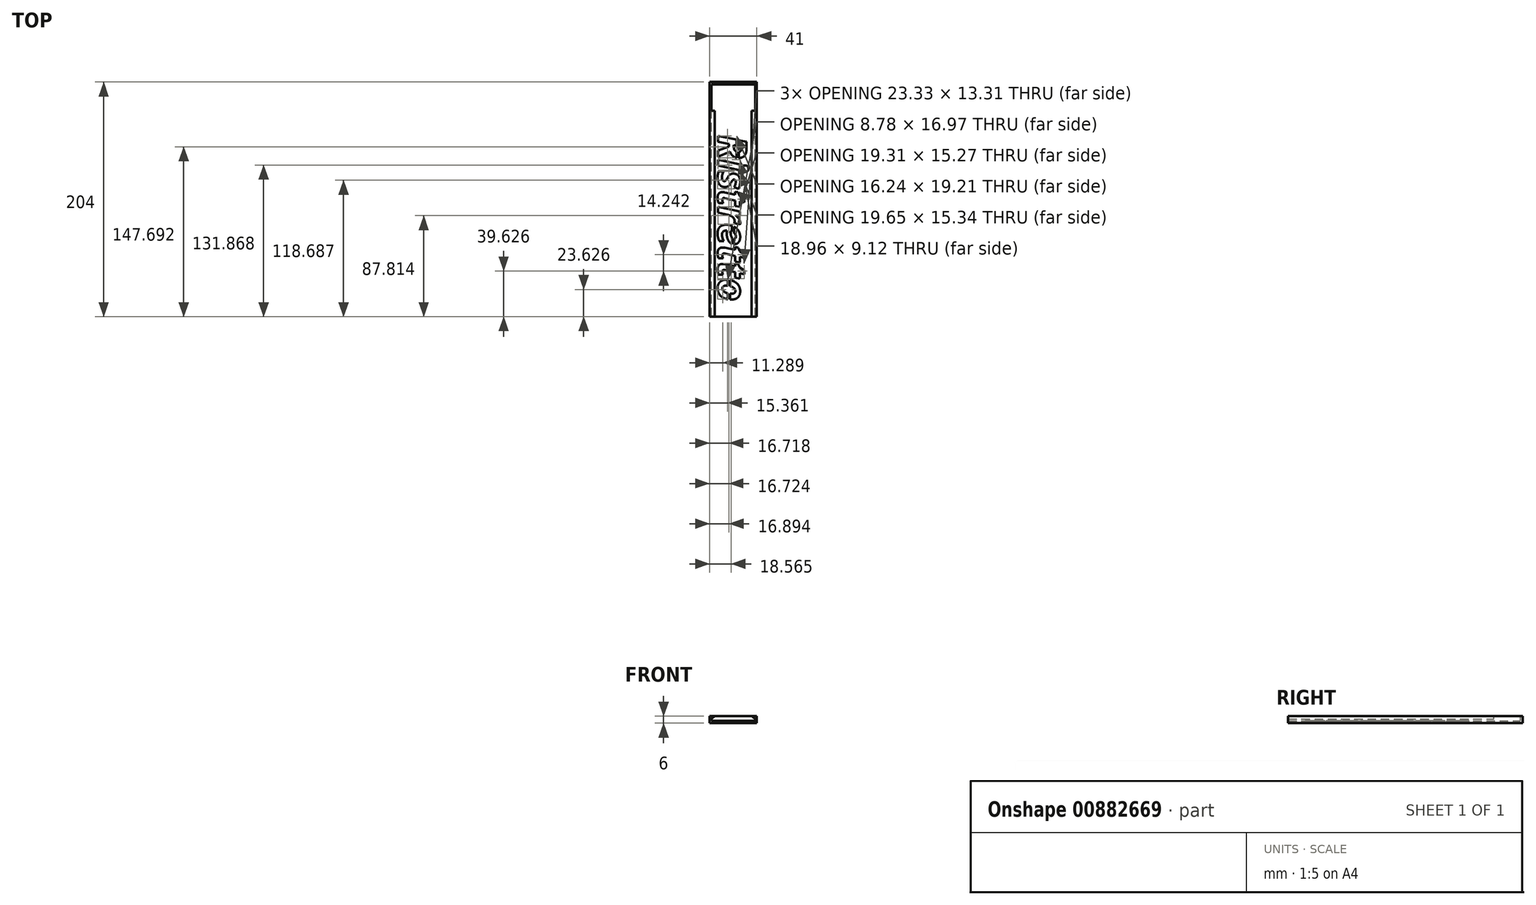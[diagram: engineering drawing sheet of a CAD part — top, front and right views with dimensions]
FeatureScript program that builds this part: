
annotation { "Feature Type Name" : "Feature", "Feature Type Description" : "" }
export const myFeature = defineFeature(function(context is Context, id is Id, definition is map)
    precondition{}
    {
        {
            var Q0;
            Q0=qCreatedBy(makeId("Front.planeOp"),FACE);
            var sketch = newSketch(context, id + "F0", { "sketchPlane" : qUnion([Q0])});
            skLineSegment(sketch, "E0", {"start": v(-20.5, 0) * mm, "end": v(20.5, 0) * mm});
            skLineSegment(sketch, "E1", {"start": v(20.5, 0) * mm, "end": v(20.5, 6) * mm});
            skLineSegment(sketch, "E2", {"start": v(20.5, 6) * mm, "end": v(16, 6) * mm});
            skLineSegment(sketch, "E3", {"start": v(19, 2) * mm, "end": v(-19, 2) * mm});
            skLineSegment(sketch, "E4", {"start": v(-16, 6) * mm, "end": v(-20.5, 6) * mm});
            skLineSegment(sketch, "E5", {"start": v(-20.5, 6) * mm, "end": v(-20.5, 0) * mm});
            skLineSegment(sketch, "E6", {"start": v(-16, 6) * mm, "end": v(16, 6) * mm});
            skLineSegment(sketch, "E7", {"start": v(16, 6) * mm, "end": v(19, 3.6) * mm});
            skLineSegment(sketch, "E8", {"start": v(19, 3.6) * mm, "end": v(19, 2) * mm});
            skLineSegment(sketch, "E9", {"start": v(-16, 6) * mm, "end": v(-19, 3.6) * mm});
            skLineSegment(sketch, "E10", {"start": v(-19, 3.6) * mm, "end": v(-19, 2) * mm});
            skSolve(sketch);
        }
        {
            var Q0;
            Q0=makeQuery(id+"F0.imprint","IMPRINT",FACE,{"disambiguationData":[TD([[makeQuery(id+"F0.imprint","IMPRINT",EDGE,{"derivedFrom":sQuery(id+"F0.wireOp",EDGE,"E0")}),1.0]])]});
            extrude(context, id + "F1", {"entities" : qUnion([Q0]), "depth" : 202 * mm, "offsetDistance" : 25 * mm});
        }
        {
            var Q0;
            Q0=qCreatedBy(makeId("Front.planeOp"),FACE);
            var sketch = newSketch(context, id + "F2", { "sketchPlane" : qUnion([Q0])});
            skLineSegment(sketch, "E11.bottom", {"start": v(20.5, 6) * mm, "end": v(-20.5, 6) * mm});
            skLineSegment(sketch, "E11.top", {"start": v(20.5, 0) * mm, "end": v(-20.5, 0) * mm});
            skLineSegment(sketch, "E11.left", {"start": v(20.5, 6) * mm, "end": v(20.5, 0) * mm});
            skLineSegment(sketch, "E11.right", {"start": v(-20.5, 6) * mm, "end": v(-20.5, 0) * mm});
            skSolve(sketch);
        }
        {
            var Q0;
            Q0=makeQuery(id+"F2.imprint","IMPRINT",FACE,{"disambiguationData":[TD([[makeQuery(id+"F2.imprint","IMPRINT",EDGE,{"derivedFrom":sQuery(id+"F2.wireOp",EDGE,"E11.bottom")}),1.0]])]});
            extrude(context, id + "F3", {"entities" : qUnion([Q0]), "operationType" : NewBodyOperationType.ADD, "oppositeDirection" : true, "depth" : 2 * mm, "offsetDistance" : 25 * mm});
        }
        {
            var Q0;
            Q0=makeQuery(id+"F3.boolean.opBoolean","MERGE",FACE,{"derivedFrom":[makeQuery(id+"F1.opExtrude","SWEPT_FACE",FACE,{"disambiguationData":[OSD([sQuery(id+"F0.wireOp",EDGE,"E2")])]}),makeQuery(id+"F1.opExtrude","SWEPT_FACE",FACE,{"disambiguationData":[OSD([sQuery(id+"F0.wireOp",EDGE,"E4")])]}),makeQuery(id+"F3.opExtrude","SWEPT_FACE",FACE,{"disambiguationData":[OSD([sQuery(id+"F2.wireOp",EDGE,"E11.bottom")])]})]});
            cPlane(context, id + "F4", {"entities" : qUnion([Q0]), "cplaneType" : CPlaneType.OFFSET, "offset" : 0 * mm, "width" : 150 * mm, "height" : 150 * mm});
        }
        {
            var Q0;
            Q0=qCreatedBy(id+"F4.planeOp",FACE);
            var sketch = newSketch(context, id + "F5", { "sketchPlane" : qUnion([Q0])});
            skLineSegment(sketch, "E12.bottom", {"start": v(19, 0) * mm, "end": v(-19, 0) * mm});
            skLineSegment(sketch, "E12.top", {"start": v(19, -23) * mm, "end": v(-19, -23) * mm});
            skLineSegment(sketch, "E12.left", {"start": v(19, 0) * mm, "end": v(19, -23) * mm});
            skLineSegment(sketch, "E12.right", {"start": v(-19, 0) * mm, "end": v(-19, -23) * mm});
            skSolve(sketch);
        }
        {
            var Q0;
            Q0=makeQuery(id+"F5.imprint","IMPRINT",FACE,{"disambiguationData":[TD([[makeQuery(id+"F5.imprint","IMPRINT",EDGE,{"derivedFrom":sQuery(id+"F5.wireOp",EDGE,"E12.bottom")}),1.0]])]});
            extrude(context, id + "F6", {"entities" : qUnion([Q0]), "operationType" : NewBodyOperationType.REMOVE, "oppositeDirection" : true, "depth" : 4 * mm, "offsetDistance" : 25 * mm});
        }
        {
            var Q0;
            Q0=qCreatedBy(id+"F4.planeOp",FACE);
            cPlane(context, id + "F7", {"entities" : qUnion([Q0]), "cplaneType" : CPlaneType.OFFSET, "offset" : 4 * mm, "oppositeDirection" : true, "width" : 150 * mm, "height" : 150 * mm});
        }
        {
            var Q0;
            Q0=qCreatedBy(id+"F7.planeOp",FACE);
            var sketch = newSketch(context, id + "F8", { "sketchPlane" : qUnion([Q0])});
            skText(sketch, "E13", { "text": "Ristretto", "fontName": "OpenSans-BoldItalic.ttf"});
            skLineSegment(sketch, "E14.bottom", {"start": v(4.98, -47.16) * mm, "end": v(2.98, -47.16) * mm});
            skLineSegment(sketch, "E14.top", {"start": v(4.98, -65.24) * mm, "end": v(2.98, -65.24) * mm});
            skLineSegment(sketch, "E14.left", {"start": v(4.98, -47.16) * mm, "end": v(4.98, -65.24) * mm});
            skLineSegment(sketch, "E14.right", {"start": v(2.98, -47.16) * mm, "end": v(2.98, -65.24) * mm});
            skLineSegment(sketch, "E15.bottom", {"start": v(0.88, -121.8) * mm, "end": v(-1.12, -121.8) * mm});
            skLineSegment(sketch, "E15.top", {"start": v(0.88, -140.85) * mm, "end": v(-1.12, -140.85) * mm});
            skLineSegment(sketch, "E15.left", {"start": v(0.88, -121.8) * mm, "end": v(0.88, -140.85) * mm});
            skLineSegment(sketch, "E15.right", {"start": v(-1.12, -121.8) * mm, "end": v(-1.12, -140.85) * mm});
            skLineSegment(sketch, "E16.bottom", {"start": v(-2.82, -169.73) * mm, "end": v(-4.82, -169.73) * mm});
            skLineSegment(sketch, "E16.top", {"start": v(-2.82, -188.1) * mm, "end": v(-4.82, -188.1) * mm});
            skLineSegment(sketch, "E16.left", {"start": v(-2.82, -169.73) * mm, "end": v(-2.82, -188.1) * mm});
            skLineSegment(sketch, "E16.right", {"start": v(-4.82, -169.73) * mm, "end": v(-4.82, -188.1) * mm});
            const initialGuessF8  = {"E13": [-0.01326, -0.0438, 0, -1, 0.025]};
            skSetInitialGuess(sketch, initialGuessF8);
            skSolve(sketch);
        }
        {
            var Q0;
            {var subQ1=sQuery(id+"F8.wireOp",EDGE,"E13.sketch_text.stroke-0");Q0=makeQuery(id+"F8.imprint","IMPRINT",FACE,{"disambiguationData":[TD([[makeQuery(id+"F8.imprint","IMPRINT",EDGE,{"derivedFrom":subQ1}),-1.0]])]});}
            var Q1;
            {var subQ7=sQuery(id+"F8.wireOp",EDGE,"E13.sketch_text.stroke-4");Q1=makeQuery(id+"F8.imprint","IMPRINT",FACE,{"disambiguationData":[TD([[makeQuery(id+"F8.imprint","IMPRINT",EDGE,{"derivedFrom":subQ7}),-1.0]])]});}
            var Q2;
            Q2=makeQuery(id+"F8.imprint","IMPRINT",FACE,{"disambiguationData":[TD([[makeQuery(id+"F8.imprint","IMPRINT",EDGE,{"derivedFrom":sQuery(id+"F8.wireOp",EDGE,"E13.sketch_text.stroke-26")}),-1.0]])]});
            var Q3;
            Q3=makeQuery(id+"F8.imprint","IMPRINT",FACE,{"disambiguationData":[TD([[makeQuery(id+"F8.imprint","IMPRINT",EDGE,{"derivedFrom":sQuery(id+"F8.wireOp",EDGE,"E13.sketch_text.stroke-19")}),-1.0]])]});
            var Q4;
            Q4=makeQuery(id+"F8.imprint","IMPRINT",FACE,{"disambiguationData":[TD([[makeQuery(id+"F8.imprint","IMPRINT",EDGE,{"derivedFrom":sQuery(id+"F8.wireOp",EDGE,"E13.sketch_text.stroke-30")}),-1.0]])]});
            var Q5;
            Q5=makeQuery(id+"F8.imprint","IMPRINT",FACE,{"disambiguationData":[TD([[makeQuery(id+"F8.imprint","IMPRINT",EDGE,{"derivedFrom":sQuery(id+"F8.wireOp",EDGE,"E13.sketch_text.stroke-53")}),-1.0]])]});
            var Q6;
            Q6=makeQuery(id+"F8.imprint","IMPRINT",FACE,{"disambiguationData":[TD([[makeQuery(id+"F8.imprint","IMPRINT",EDGE,{"derivedFrom":sQuery(id+"F8.wireOp",EDGE,"E13.sketch_text.stroke-72")}),-1.0]])]});
            var Q7;
            {var subQ7=sQuery(id+"F8.wireOp",EDGE,"E13.sketch_text.stroke-86");Q7=makeQuery(id+"F8.imprint","IMPRINT",FACE,{"disambiguationData":[TD([[makeQuery(id+"F8.imprint","IMPRINT",EDGE,{"derivedFrom":subQ7}),-1.0]])]});}
            var Q8;
            {var subQ1=sQuery(id+"F8.wireOp",EDGE,"E13.sketch_text.stroke-84");Q8=makeQuery(id+"F8.imprint","IMPRINT",FACE,{"disambiguationData":[TD([[makeQuery(id+"F8.imprint","IMPRINT",EDGE,{"derivedFrom":subQ1}),-1.0]])]});}
            var Q9;
            Q9=makeQuery(id+"F8.imprint","IMPRINT",FACE,{"disambiguationData":[TD([[makeQuery(id+"F8.imprint","IMPRINT",EDGE,{"derivedFrom":sQuery(id+"F8.wireOp",EDGE,"E13.sketch_text.stroke-108")}),-1.0]])]});
            var Q10;
            Q10=makeQuery(id+"F8.imprint","IMPRINT",FACE,{"disambiguationData":[TD([[makeQuery(id+"F8.imprint","IMPRINT",EDGE,{"derivedFrom":sQuery(id+"F8.wireOp",EDGE,"E13.sketch_text.stroke-127")}),-1.0]])]});
            var Q11;
            {var subQ7=sQuery(id+"F8.wireOp",EDGE,"E13.sketch_text.stroke-150");Q11=makeQuery(id+"F8.imprint","IMPRINT",FACE,{"disambiguationData":[TD([[makeQuery(id+"F8.imprint","IMPRINT",EDGE,{"derivedFrom":subQ7}),-1.0]])]});}
            var Q12;
            {var subQ5=sQuery(id+"F8.wireOp",EDGE,"E13.sketch_text.stroke-146");Q12=makeQuery(id+"F8.imprint","IMPRINT",FACE,{"disambiguationData":[TD([[makeQuery(id+"F8.imprint","IMPRINT",EDGE,{"derivedFrom":subQ5}),-1.0]])]});}
            var Q13;
            Q13=makeQuery(id+"F3.boolean.opBoolean","MERGE",FACE,{"derivedFrom":[makeQuery(id+"F1.opExtrude","SWEPT_FACE",FACE,{"disambiguationData":[OSD([sQuery(id+"F0.wireOp",EDGE,"E0")])]}),makeQuery(id+"F3.opExtrude","SWEPT_FACE",FACE,{"disambiguationData":[OSD([sQuery(id+"F2.wireOp",EDGE,"E11.top")])]})]});
            extrude(context, id + "F9", {"entities" : qUnion([Q0, Q1, Q2, Q3, Q4, Q5, Q6, Q7, Q8, Q9, Q10, Q11, Q12]), "operationType" : NewBodyOperationType.REMOVE, "endBound" : BoundingType.UP_TO_SURFACE, "oppositeDirection" : true, "depth" : 25 * mm, "endBoundEntityFace" : qUnion([Q13]), "offsetDistance" : 25 * mm});
        }
    });
